# Revit family: Sink-Service_Sink-KOHLER-Whitby-K-6710
name_source: partatom
category: Plumbing Fixtures
revit_build: Autodesk Revit 2015 (Build: 20140606_1530(x64)
units: mm (PartAtom-declared; Revit-internal decimal feet)

## types (1)
- 0-White
    ADA Compliant = No
    Assembly Code = D2010400
    CW Connection = No
    Cold Water Inlet = Cold Water Inlet
    Date Modified = 10/19/2018
    Default Elevation = 0"
    Description = Floor-mounted corner service sink
    Drain Included = No
    Environmental Product Declaration = https://www.us.kohler.com
    Finish = Kohler-Vitreous_China-0-White
    HW Connection = No
    Height = 13"
    Hot Water Inlet = Hot Water Inlet
    Length = 28"
    Manufacturer = KOHLER Co.
    MasterFormat 1995 = 15410
    MasterFormat 2004 = 22.41.16
    Material = Enameled Cast Iron
    Model = K-6710
    Product Documentation Link = https://www.us.kohler.com
    Product Name = Whitby
    Product Page URL = http://www.us.kohler.com
    URL = https://www.us.kohler.com
    Vent Connection = No
    Waste Connection = Yes
    Waste Water Outlet = Waste Water Outlet
    Width = 28"

## geometry (parser evidence)
native form markers: Blend x2, Sweep x5
no freeform markers — native parametric forms only
